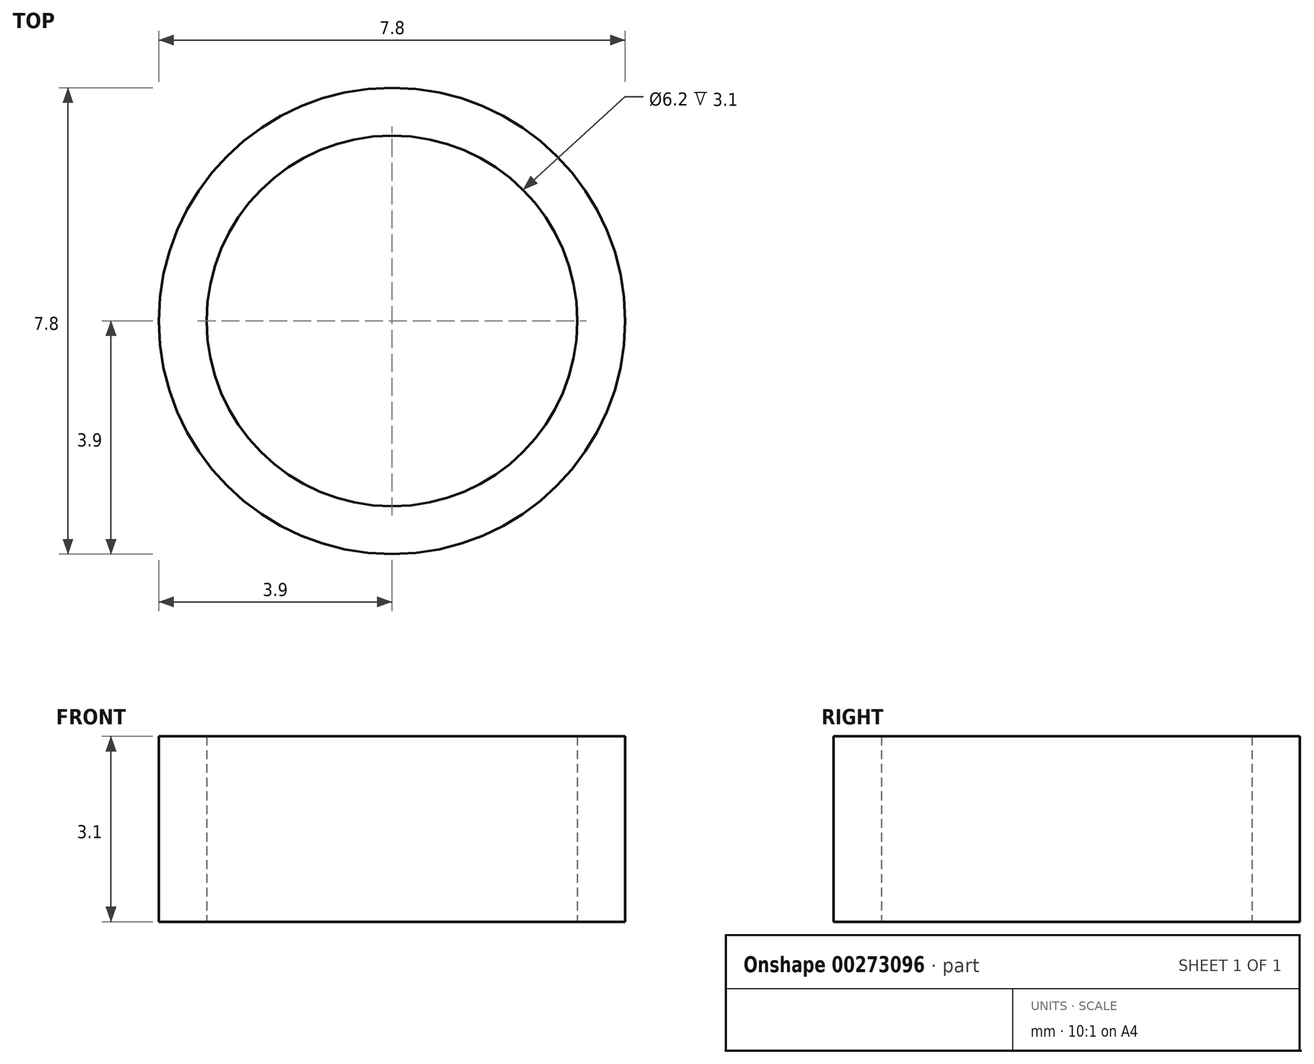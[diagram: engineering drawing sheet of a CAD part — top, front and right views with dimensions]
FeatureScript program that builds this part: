
annotation { "Feature Type Name" : "Feature", "Feature Type Description" : "" }
export const myFeature = defineFeature(function(context is Context, id is Id, definition is map)
    precondition{}
    {
        {
            var Q0;
            Q0=qCreatedBy(makeId("Top.planeOp"),FACE);
            var sketch = newSketch(context, id + "F0", { "sketchPlane" : qUnion([Q0])});
            skCircle(sketch, "E0", {"center": v(0, 0) * mm, "radius": 3.1 * mm});
            skCircle(sketch, "E1", {"center": v(0, 0) * mm, "radius": 3.9 * mm});
            skSolve(sketch);
        }
        {
            var Q0;
            Q0=makeQuery(id+"F0.imprint","IMPRINT",FACE,{"disambiguationData":[TD([[makeQuery(id+"F0.imprint","IMPRINT",EDGE,{"derivedFrom":sQuery(id+"F0.wireOp",EDGE,"E0")}),-1.0]])]});
            extrude(context, id + "F1", {"entities" : qUnion([Q0]), "depth" : 3.1 * mm});
        }
    });
